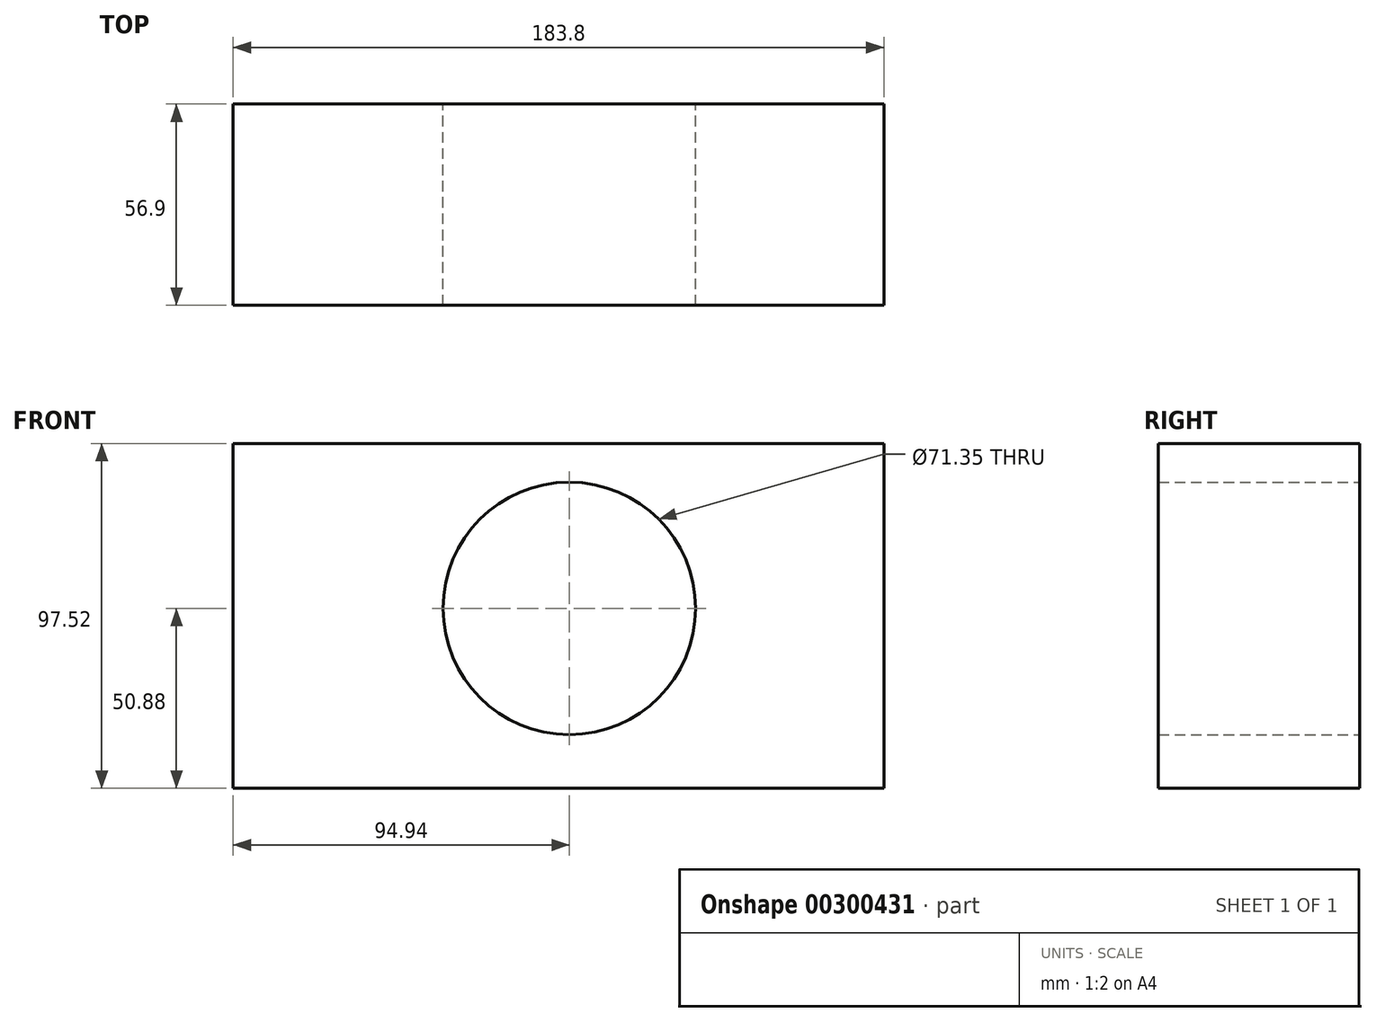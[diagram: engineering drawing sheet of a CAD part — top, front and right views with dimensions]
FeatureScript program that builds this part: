
annotation { "Feature Type Name" : "Feature", "Feature Type Description" : "" }
export const myFeature = defineFeature(function(context is Context, id is Id, definition is map)
    precondition{}
    {
        {
            var Q0;
            Q0=qCreatedBy(makeId("Front.planeOp"),FACE);
            var sketch = newSketch(context, id + "F0", { "sketchPlane" : qUnion([Q0])});
            skLineSegment(sketch, "E0.bottom", {"start": v(-94.94, 46.64) * mm, "end": v(88.86, 46.64) * mm});
            skLineSegment(sketch, "E0.top", {"start": v(-94.94, -50.88) * mm, "end": v(88.86, -50.88) * mm});
            skLineSegment(sketch, "E0.left", {"start": v(-94.94, 46.64) * mm, "end": v(-94.94, -50.88) * mm});
            skLineSegment(sketch, "E0.right", {"start": v(88.86, 46.64) * mm, "end": v(88.86, -50.88) * mm});
            skCircle(sketch, "E1", {"center": v(0, 0) * mm, "radius": 35.67 * mm});
            skSolve(sketch);
        }
        {
            var Q0;
            Q0 = qSketchRegion(id + "F0", true);
            extrude(context, id + "F1", {"entities" : qUnion([Q0]), "depth" : 56.9 * mm});
        }
    });
